# Revit family: Domotics-SerieCivili-GEWISS-27COMBI_SYSTEM-IP55_TESTA_PALO
name_source: partatom
category: Apparecchi elettrici
revit_build: Autodesk Revit 2016 (Build: 20161004_0715(x64)
units: mm (PartAtom-declared; Revit-internal decimal feet)

## family parameters
Condiviso = No
Host = Superficie
Mantenere orientamento annotazione = No
Numero OmniClass = 23.80.30.14.24
Punto di calcolo locali = No
Quota connettore circolare = Usa diametro
Taglio con vuoti quando caricato = Sì
Tipo di parte = Normale
Titolo OmniClass = Junction Boxes

## types (1)
- Domotics-SerieCivili-GEWISS-27COMBI_SYSTEM-IP55_TESTA_PALO
    Catalogo = DOMOTICS
    Catalogo Serie = 27COMBI
    Classe isolamento = II
    Codice EAN = 8011564055421
    Codice Electrocod = 0212
    Colore = Grigio RAL 7035
    Colore portella = Trasparente
    Coppia serraggio viti = 0,8NM
    Descrizione = CONT.3 POSTI STAGNO FISS.TESTA PALO
    Descrizione: = 3 posti
    Dim. esterne BxHxP (mm) = 122x149x85
    Fissaggio = Testa palo
    Glow Wire Test = 650°C
    Grado di protezione = IP55
    IDF = a400302d-f7e7-4da5-b7d5-d8016424dfc8
    IDT = 95c7bd8d-86a8-4c38-ba26-845f677c2e43
    Immagine tipo = gw27056.jpg
    Modello = GW27056
    N. fori aperti = 1
    N. moduli SYSTEM = 3 posti
    Norma di riferimento: = EN 60670-1
    Offset = 0 mm  [stored 0 ft]
    Per pali Ã˜ = 54-60MM
    Produttore = GEWISS S.p.A.
    Prospetto di default = 1219 mm
    Resistenza agli urti = IK07
    SEO = Contenitore
    Scheda Tecnica = https://www.gewiss.com
    Temperatura di installazione = -25 +60 °C
    Termopressione con biglia = 70 °C
    Tipo portella = Con membrana
    URL = https://www.gewiss.com
    Versione file RFA = 19.4
    Viti coperchio = Acciaio inox

note: [stored X ft] marks values corroborated as IEEE doubles in the binary element streams (Revit-internal decimal feet)
